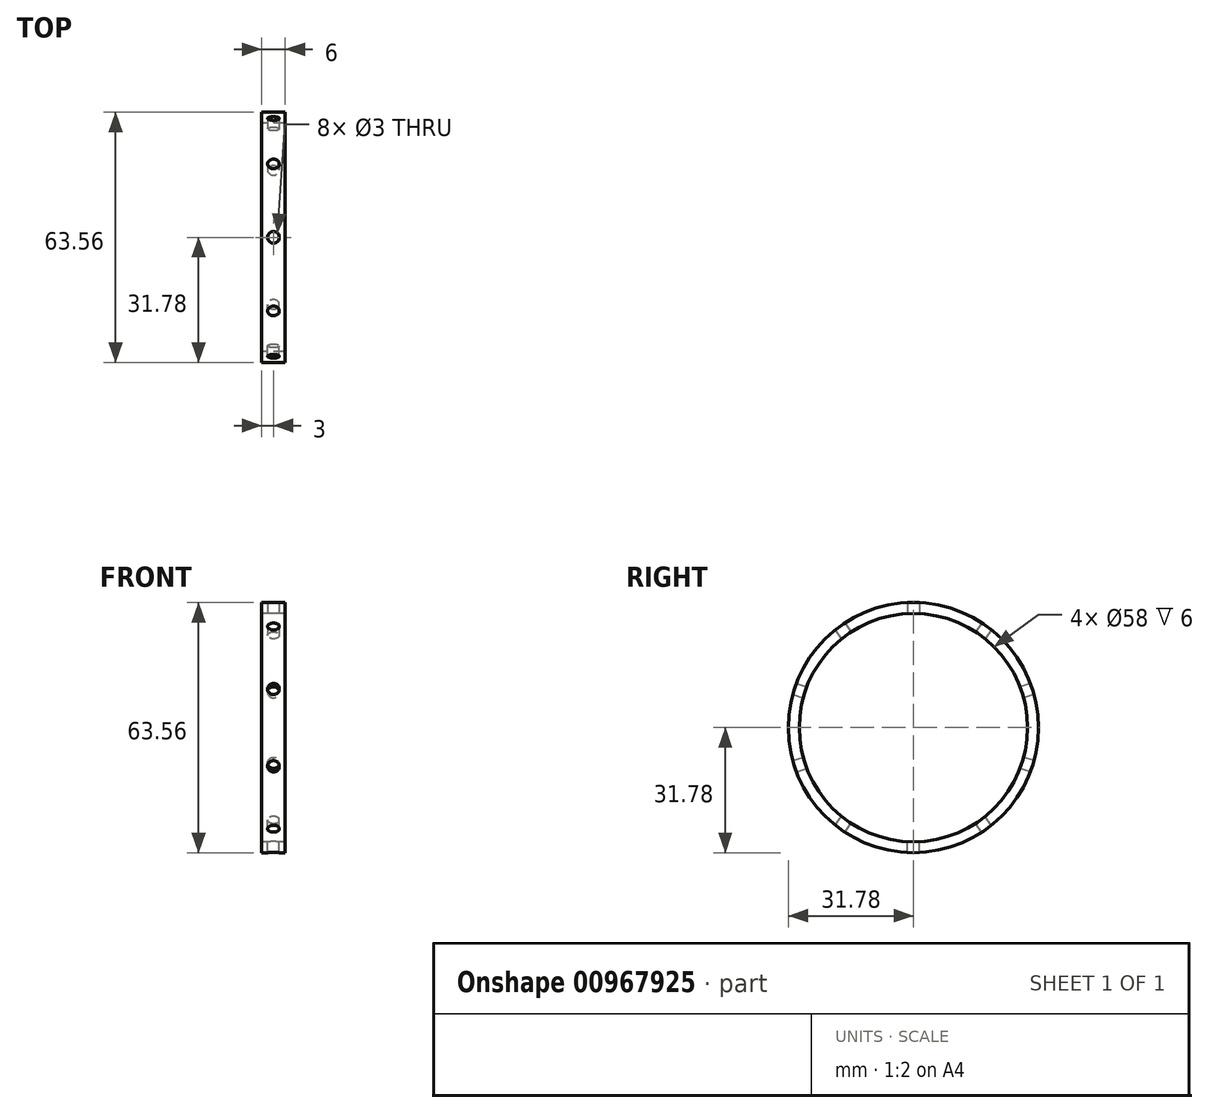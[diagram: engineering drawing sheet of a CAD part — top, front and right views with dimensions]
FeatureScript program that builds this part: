
annotation { "Feature Type Name" : "Feature", "Feature Type Description" : "" }
export const myFeature = defineFeature(function(context is Context, id is Id, definition is map)
    precondition{}
    {
        {
            var Q0;
            Q0=qCreatedBy(makeId("Right.planeOp"),FACE);
            var sketch = newSketch(context, id + "F0", { "sketchPlane" : qUnion([Q0])});
            skCircle(sketch, "E0", {"center": v(0, 0) * mm, "radius": 31.77 * mm});
            skCircle(sketch, "E1", {"center": v(0, 0) * mm, "radius": 29 * mm});
            skSolve(sketch);
        }
        {
            var Q0;
            Q0=makeQuery(id+"F0.imprint","IMPRINT",FACE,{"disambiguationData":[TD([[makeQuery(id+"F0.imprint","IMPRINT",EDGE,{"derivedFrom":sQuery(id+"F0.wireOp",EDGE,"E0")}),1.0]])]});
            extrude(context, id + "F1", {"entities" : qUnion([Q0]), "depth" : 6 * mm, "offsetDistance" : 25 * mm, "symmetric" : true});
        }
        {
            var Q0;
            Q0=qCreatedBy(makeId("Top.planeOp"),FACE);
            var sketch = newSketch(context, id + "F2", { "sketchPlane" : qUnion([Q0])});
            skCircle(sketch, "E2", {"center": v(0, 0) * mm, "radius": 1.5 * mm});
            skLineSegment(sketch, "E3", {"start": v(0, 0) * mm, "end": v(-18.97, 0) * mm});
            skSolve(sketch);
        }
        {
            var Q0;
            Q0=makeQuery(id+"F2.imprint","IMPRINT",FACE,{"disambiguationData":[TD([[makeQuery(id+"F2.imprint","IMPRINT",EDGE,{"derivedFrom":sQuery(id+"F2.wireOp",EDGE,"E2")}),1.0]])]});
            extrude(context, id + "F3", {"entities" : qUnion([Q0]), "depth" : 50.4 * mm, "offsetDistance" : 25 * mm, "hasSecondDirection" : true, "secondDirectionOppositeDirection" : false, "secondDirectionDepth" : 19.1 * mm});
        }
        {
            var Q0;
            Q0=makeQuery(id+"F3.opExtrude","SWEPT_BODY",BODY,{"disambiguationData":[OSD([sQuery(id+"F2.wireOp",EDGE,"E2")])]});
            var Q1;
            Q1=sQuery(id+"F2.wireOp",EDGE,"E3");
            circularPattern(context, id + "F4", {"operationType" : NewBodyOperationType.REMOVE, "entities" : qUnion([Q0]), "axis" : qUnion([Q1]), "angle" : 360 * degree, "instanceCount" : 10, "equalSpace" : true});
        }
    });
